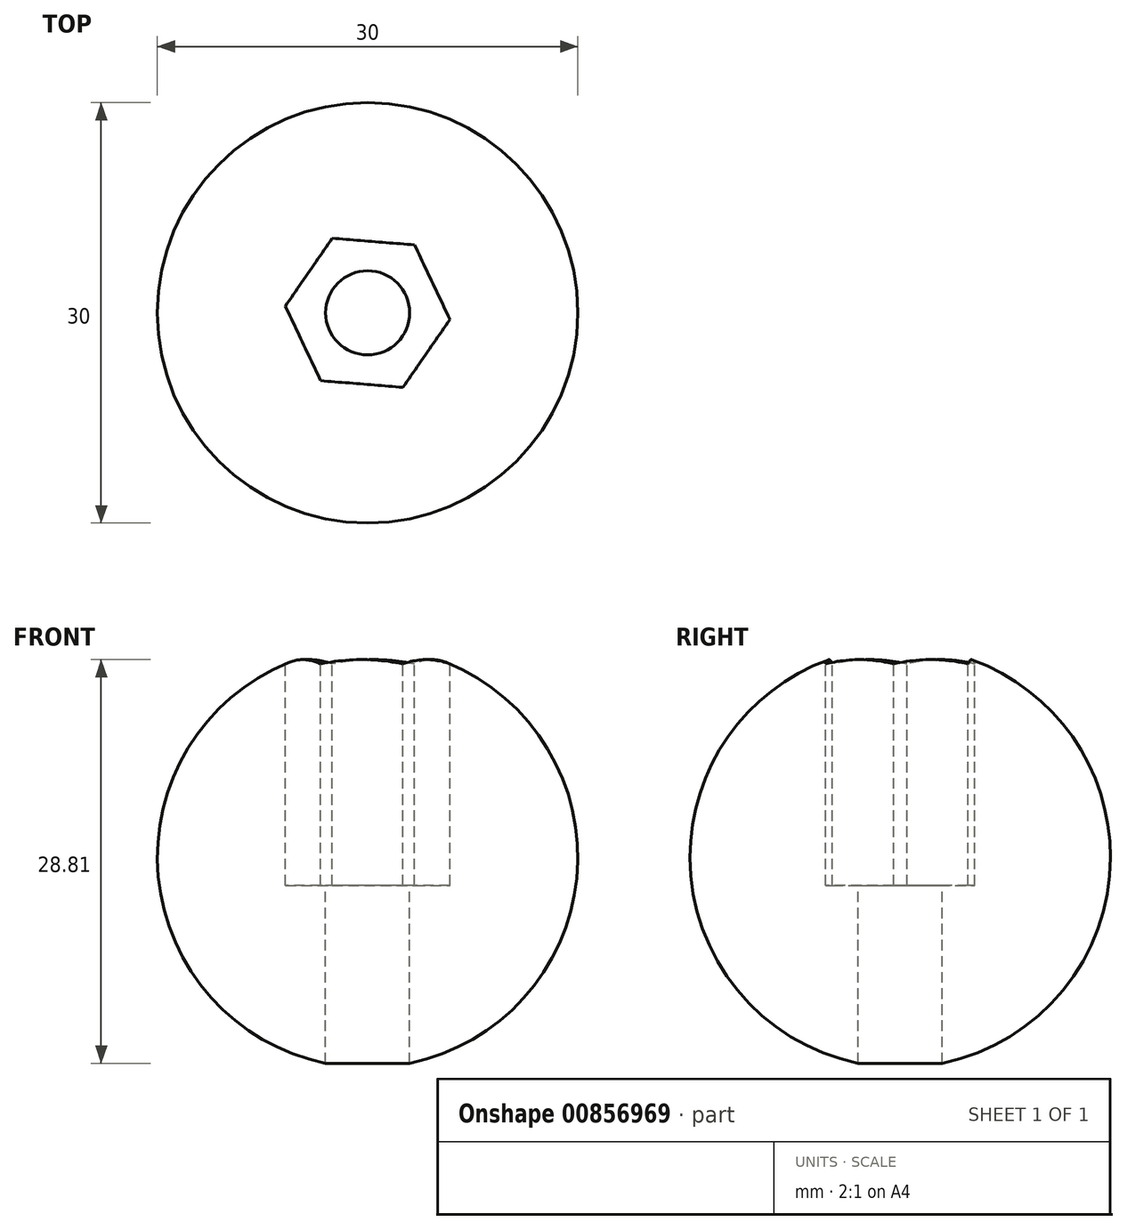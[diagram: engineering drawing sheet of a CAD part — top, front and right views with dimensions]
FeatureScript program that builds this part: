
annotation { "Feature Type Name" : "Feature", "Feature Type Description" : "" }
export const myFeature = defineFeature(function(context is Context, id is Id, definition is map)
    precondition{}
    {
        {
            var Q0;
            Q0=qCreatedBy(makeId("Top.planeOp"),FACE);
            var sketch = newSketch(context, id + "F0", { "sketchPlane" : qUnion([Q0])});
            skLineSegment(sketch, "E0", {"start": v(0, 15) * mm, "end": v(0, -15) * mm});
            skArc(sketch, "E1", {"start": v(0, -15) * mm, "mid": v(15, 0) * mm, "end": v(0, 15) * mm});
            skSolve(sketch);
        }
        {
            var Q0;
            Q0=makeQuery(id+"F0.imprint","IMPRINT",FACE,{"disambiguationData":[TD([[makeQuery(id+"F0.imprint","IMPRINT",EDGE,{"derivedFrom":sQuery(id+"F0.wireOp",EDGE,"E0")}),1.0]])]});
            var Q1;
            Q1=sQuery(id+"F0.wireOp",EDGE,"E0");
            revolve(context, id + "F1", {"surfaceOperationType" : NewSurfaceOperationType.NEW, "entities" : qUnion([Q0]), "axis" : qUnion([Q1]), "revolveType" : RevolveType.FULL});
        }
        {
            var Q0;
            Q0=qCreatedBy(makeId("Top.planeOp"),FACE);
            cPlane(context, id + "F2", {"entities" : qUnion([Q0]), "cplaneType" : CPlaneType.OFFSET, "offset" : 20 * mm, "width" : 150 * mm, "height" : 150 * mm});
        }
        {
            var Q0;
            Q0=qCreatedBy(id+"F2.planeOp",FACE);
            var sketch = newSketch(context, id + "F3", { "sketchPlane" : qUnion([Q0])});
            skCircle(sketch, "E2.cCircle", {"center": v(0, 0) * mm, "radius": 5.1 * mm, "construction": true});
            skLineSegment(sketch, "E2.0", {"start": v(5.87, -0.48) * mm, "end": v(2.52, -5.32) * mm});
            skLineSegment(sketch, "E2.1", {"start": v(2.52, -5.32) * mm, "end": v(-3.35, -4.85) * mm});
            skLineSegment(sketch, "E2.2", {"start": v(-3.35, -4.85) * mm, "end": v(-5.87, 0.48) * mm});
            skLineSegment(sketch, "E2.3", {"start": v(-5.87, 0.48) * mm, "end": v(-2.52, 5.32) * mm});
            skLineSegment(sketch, "E2.4", {"start": v(-2.52, 5.32) * mm, "end": v(3.35, 4.85) * mm});
            skLineSegment(sketch, "E2.5", {"start": v(3.35, 4.85) * mm, "end": v(5.87, -0.48) * mm});
            skPoint(sketch, "E2.0.midPoint", {"position": v(4.2, -2.9) * mm});
            skSolve(sketch);
        }
        {
            var Q0;
            Q0=makeQuery(id+"F3.imprint","IMPRINT",FACE,{"disambiguationData":[TD([[makeQuery(id+"F3.imprint","IMPRINT",EDGE,{"derivedFrom":sQuery(id+"F3.wireOp",EDGE,"E2.0")}),-1.0]])]});
            extrude(context, id + "F4", {"entities" : qUnion([Q0]), "operationType" : NewBodyOperationType.REMOVE, "oppositeDirection" : true, "depth" : 22 * mm, "offsetDistance" : 25 * mm});
        }
        {
            var Q0;
            Q0=qCreatedBy(id+"F2.planeOp",FACE);
            var sketch = newSketch(context, id + "F5", { "sketchPlane" : qUnion([Q0])});
            skCircle(sketch, "E3", {"center": v(0, 0) * mm, "radius": 3 * mm});
            skSolve(sketch);
        }
        {
            var Q0;
            Q0=makeQuery(id+"F5.imprint","IMPRINT",FACE,{"disambiguationData":[TD([[makeQuery(id+"F5.imprint","IMPRINT",EDGE,{"derivedFrom":sQuery(id+"F5.wireOp",EDGE,"E3")}),1.0]])]});
            extrude(context, id + "F6", {"entities" : qUnion([Q0]), "operationType" : NewBodyOperationType.REMOVE, "endBound" : BoundingType.THROUGH_ALL, "oppositeDirection" : true, "depth" : 25 * mm, "offsetDistance" : 25 * mm});
        }
    });
